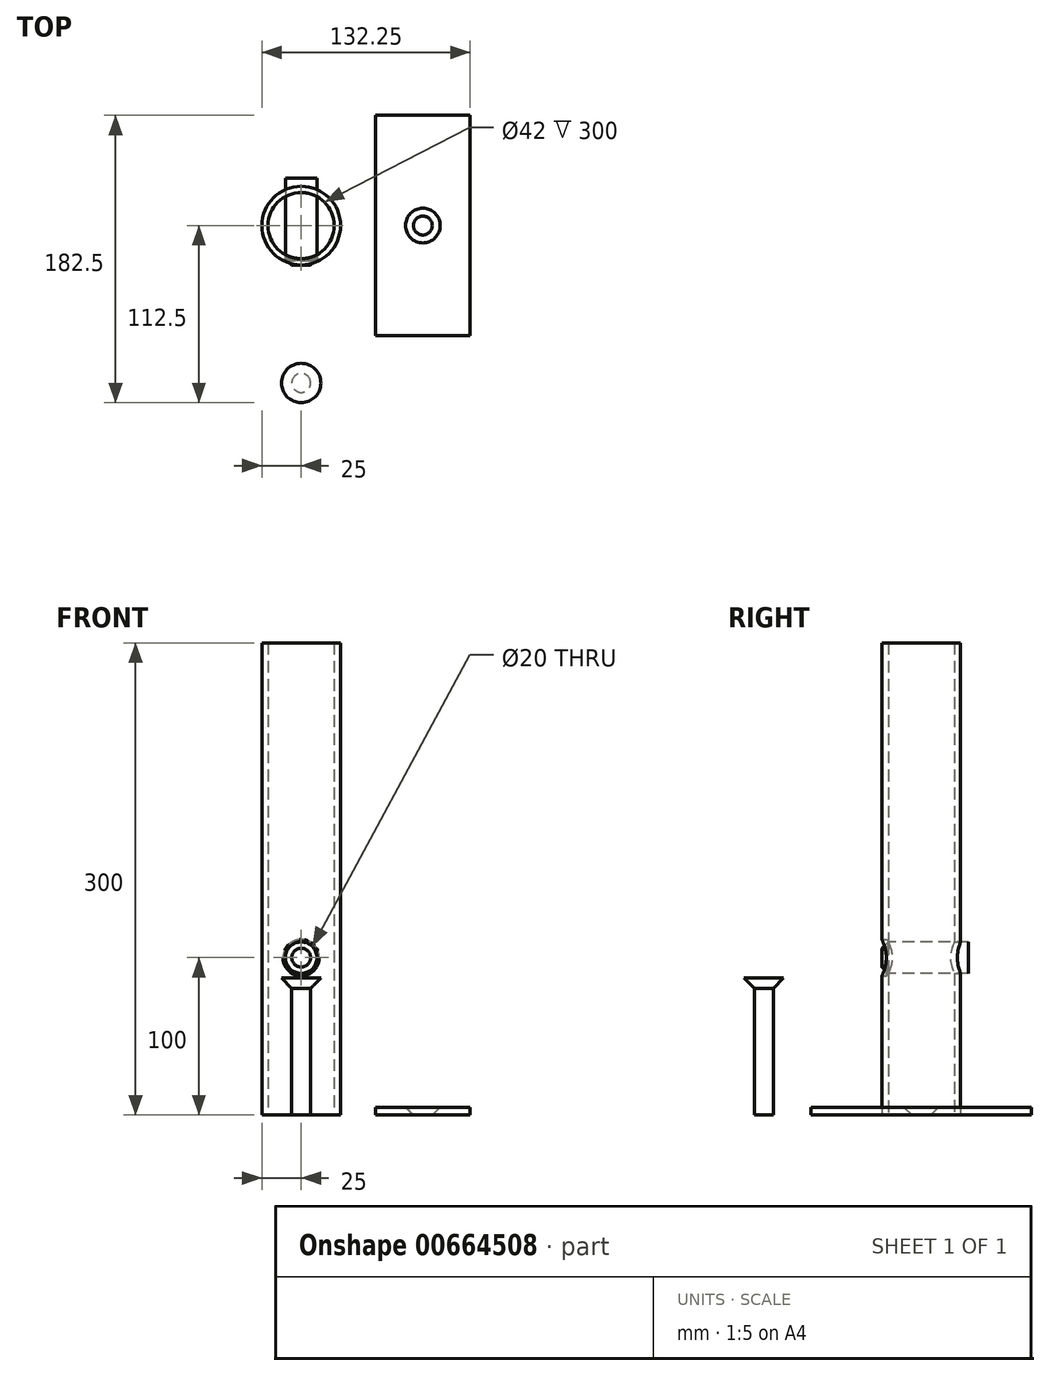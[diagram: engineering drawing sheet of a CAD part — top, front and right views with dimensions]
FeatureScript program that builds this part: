
annotation { "Feature Type Name" : "Feature", "Feature Type Description" : "" }
export const myFeature = defineFeature(function(context is Context, id is Id, definition is map)
    precondition{}
    {
        {
            var Q0;
            Q0=qCreatedBy(makeId("Top.planeOp"),FACE);
            var sketch = newSketch(context, id + "F0", { "sketchPlane" : qUnion([Q0])});
            skCircle(sketch, "E0", {"center": v(0, 0) * mm, "radius": 21 * mm});
            skCircle(sketch, "E1", {"center": v(0, 0) * mm, "radius": 25 * mm});
            skSolve(sketch);
        }
        {
            var Q0;
            Q0=makeQuery(id+"F0.imprint","IMPRINT",FACE,{"disambiguationData":[TD([[makeQuery(id+"F0.imprint","IMPRINT",EDGE,{"derivedFrom":sQuery(id+"F0.wireOp",EDGE,"E0")}),-1.0]])]});
            extrude(context, id + "F1", {"entities" : qUnion([Q0]), "depth" : 300 * mm, "offsetDistance" : 25 * mm});
        }
        {
            var Q0;
            Q0=qCreatedBy(makeId("Front.planeOp"),FACE);
            cPlane(context, id + "F2", {"entities" : qUnion([Q0]), "cplaneType" : CPlaneType.OFFSET, "offset" : 25 * mm, "width" : 150 * mm, "height" : 150 * mm});
        }
        {
            var Q0;
            Q0=qCreatedBy(id+"F2.planeOp",FACE);
            var sketch = newSketch(context, id + "F3", { "sketchPlane" : qUnion([Q0])});
            skLineSegment(sketch, "E2", {"start": v(0, 0) * mm, "end": v(0, 100) * mm});
            skCircle(sketch, "E3", {"center": v(0, 100) * mm, "radius": 10 * mm});
            skSolve(sketch);
        }
        {
            var Q0;
            Q0=sQuery(id+"F3.wireOp",VERTEX,"E2.end");
            var Q1;
            Q1=makeQuery(id+"F1.opExtrude","SWEPT_BODY",BODY,{"disambiguationData":[OSD([sQuery(id+"F0.wireOp",EDGE,"E0"),sQuery(id+"F0.wireOp",EDGE,"E1")])]});
            hole(context, id + "F4", {"style" : HoleStyle.C_SINK, "endStyle" : HoleEndStyle.THROUGH, "holeDiameter" : 20 * mm, "cSinkDiameter" : 23 * mm, "cSinkAngle" : 90 * degree, "majorDiameter" : 5 * mm, "isTappedThrough" : true, "tappedDepth" : 12 * mm, "tapClearance" : 3, "locations" : qUnion([Q0]), "scope" : qUnion([Q1])});
        }
        {
            var Q0;
            Q0=makeQuery(id+"F3.imprint","IMPRINT",FACE,{"disambiguationData":[TD([[makeQuery(id+"F3.imprint","IMPRINT",EDGE,{"derivedFrom":sQuery(id+"F3.wireOp",EDGE,"E3")}),1.0]])]});
            extrude(context, id + "F5", {"entities" : qUnion([Q0]), "oppositeDirection" : true, "depth" : 55 * mm, "offsetDistance" : 25 * mm});
        }
        {
            var Q0;
            Q0=makeQuery(id+"F5.opExtrude","CAP_EDGE",EDGE,{"disambiguationData":[OSD([sQuery(id+"F3.wireOp",EDGE,"E3")])],"isStart":true});
            chamfer(context, id + "F6", {"entities" : qUnion([Q0]), "width" : 4 * mm, "tangentPropagation" : true});
        }
        {
            var Q0;
            Q0=qCreatedBy(makeId("Top.planeOp"),FACE);
            var sketch = newSketch(context, id + "F7", { "sketchPlane" : qUnion([Q0])});
            skLineSegment(sketch, "E4", {"start": v(0, 0) * mm, "end": v(0, -100) * mm});
            skCircle(sketch, "E5", {"center": v(0, -100) * mm, "radius": 6 * mm});
            skSolve(sketch);
        }
        {
            var Q0;
            Q0=makeQuery(id+"F7.imprint","IMPRINT",FACE,{"disambiguationData":[TD([[makeQuery(id+"F7.imprint","IMPRINT",EDGE,{"derivedFrom":sQuery(id+"F7.wireOp",EDGE,"E5")}),1.0]])]});
            extrude(context, id + "F8", {"entities" : qUnion([Q0]), "depth" : 80 * mm, "offsetDistance" : 25 * mm});
        }
        {
            var Q0;
            Q0=makeQuery(id+"F8.opExtrude","CAP_FACE",FACE,{"disambiguationData":[OSD([sQuery(id+"F7.wireOp",EDGE,"E5")])],"isStart":false});
            var sketch = newSketch(context, id + "F9", { "sketchPlane" : qUnion([Q0])});
            skCircle(sketch, "E6", {"center": v(0, -100) * mm, "radius": 12.5 * mm});
            skSolve(sketch);
        }
        {
            var Q0;
            Q0 = qSketchRegion(id + "F9", true);
            extrude(context, id + "F10", {"entities" : qUnion([Q0]), "operationType" : NewBodyOperationType.ADD, "depth" : 25 * mm, "offsetDistance" : 25 * mm});
        }
        {
            var Q0;
            Q0=makeQuery(id+"F10.opExtrude","CAP_EDGE",EDGE,{"disambiguationData":[OSD([sQuery(id+"F9.wireOp",EDGE,"E6")])],"isStart":true});
            chamfer(context, id + "F11", {"entities" : qUnion([Q0]), "width" : 7 * mm, "tangentPropagation" : true});
        }
        {
            var Q0;
            Q0=makeQuery(id+"F10.opExtrude","CAP_FACE",FACE,{"disambiguationData":[OSD([sQuery(id+"F9.wireOp",EDGE,"E6")])],"isStart":false});
            extrude(context, id + "F12", {"entities" : qUnion([Q0]), "operationType" : NewBodyOperationType.REMOVE, "oppositeDirection" : true, "depth" : 18 * mm, "offsetDistance" : 25 * mm});
        }
        {
            var Q0;
            Q0=qCreatedBy(makeId("Top.planeOp"),FACE);
            var sketch = newSketch(context, id + "F13", { "sketchPlane" : qUnion([Q0])});
            skLineSegment(sketch, "E7", {"start": v(0, 0) * mm, "end": v(77.25, 0) * mm});
            skLineSegment(sketch, "E8.bottom", {"start": v(107.25, -70) * mm, "end": v(47.25, -70) * mm});
            skLineSegment(sketch, "E8.top", {"start": v(107.25, 70) * mm, "end": v(47.25, 70) * mm});
            skLineSegment(sketch, "E8.left", {"start": v(107.25, -70) * mm, "end": v(107.25, 70) * mm});
            skLineSegment(sketch, "E8.right", {"start": v(47.25, -70) * mm, "end": v(47.25, 70) * mm});
            skPoint(sketch, "E8.middle", {"position": v(77.25, 0) * mm});
            skSolve(sketch);
        }
        {
            var Q0;
            Q0 = qSketchRegion(id + "F13", true);
            extrude(context, id + "F14", {"entities" : qUnion([Q0]), "depth" : 5 * mm, "offsetDistance" : 25 * mm});
        }
        {
            var Q0;
            Q0=makeQuery(id+"F14.opExtrude","CAP_FACE",FACE,{"disambiguationData":[OSD([sQuery(id+"F13.wireOp",EDGE,"E8.bottom"),sQuery(id+"F13.wireOp",EDGE,"E8.top"),sQuery(id+"F13.wireOp",EDGE,"E8.left"),sQuery(id+"F13.wireOp",EDGE,"E8.right")])],"isStart":false});
            var sketch = newSketch(context, id + "F15", { "sketchPlane" : qUnion([Q0])});
            skCircle(sketch, "E9", {"center": v(77.25, 0) * mm, "radius": 15.73 * mm});
            skPoint(sketch, "E9.centerSnap0", {"position": v(77.25, -70) * mm});
            skPoint(sketch, "E9.centerSnap1", {"position": v(107.25, 0) * mm});
            skSolve(sketch);
        }
        {
            var Q0;
            Q0=sQuery(id+"F15.wireOp",VERTEX,"E9.center");
            var Q1;
            Q1=makeQuery(id+"F14.opExtrude","SWEPT_BODY",BODY,{"disambiguationData":[OSD([sQuery(id+"F13.wireOp",EDGE,"E8.bottom"),sQuery(id+"F13.wireOp",EDGE,"E8.top"),sQuery(id+"F13.wireOp",EDGE,"E8.left"),sQuery(id+"F13.wireOp",EDGE,"E8.right")])]});
            hole(context, id + "F16", {"style" : HoleStyle.C_SINK, "endStyle" : HoleEndStyle.THROUGH, "holeDiameter" : 12 * mm, "cSinkDiameter" : 22 * mm, "cSinkAngle" : 90 * degree, "majorDiameter" : 5 * mm, "isTappedThrough" : true, "tappedDepth" : 12 * mm, "tapClearance" : 3, "locations" : qUnion([Q0]), "scope" : qUnion([Q1])});
        }
    });
